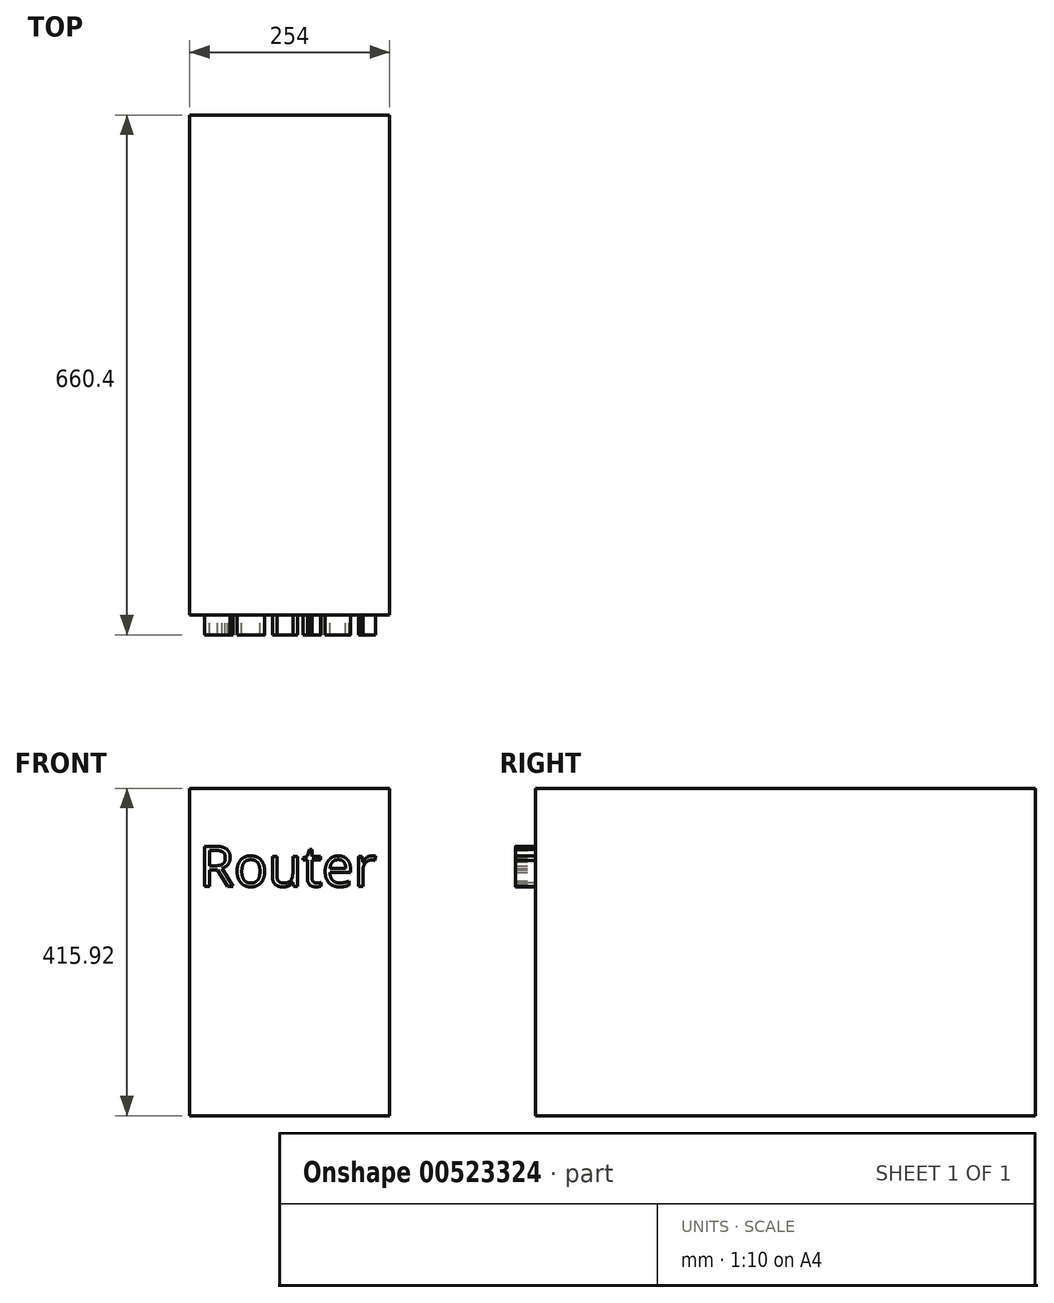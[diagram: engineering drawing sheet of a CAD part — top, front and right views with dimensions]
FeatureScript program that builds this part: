
annotation { "Feature Type Name" : "Feature", "Feature Type Description" : "" }
export const myFeature = defineFeature(function(context is Context, id is Id, definition is map)
    precondition{}
    {
        {
            var Q0;
            Q0=qCreatedBy(makeId("Front.planeOp"),FACE);
            var sketch = newSketch(context, id + "F0", { "sketchPlane" : qUnion([Q0])});
            skLineSegment(sketch, "E0.bottom", {"start": v(127, 207.96) * mm, "end": v(-127, 207.96) * mm});
            skLineSegment(sketch, "E0.top", {"start": v(127, -207.96) * mm, "end": v(-127, -207.96) * mm});
            skLineSegment(sketch, "E0.left", {"start": v(127, 207.96) * mm, "end": v(127, -207.96) * mm});
            skLineSegment(sketch, "E0.right", {"start": v(-127, 207.96) * mm, "end": v(-127, -207.96) * mm});
            skPoint(sketch, "E0.middle", {"position": v(0, 0) * mm});
            skSolve(sketch);
        }
        {
            var Q0;
            Q0=makeQuery(id+"F0.imprint","IMPRINT",FACE,{"disambiguationData":[TD([[makeQuery(id+"F0.imprint","IMPRINT",EDGE,{"derivedFrom":sQuery(id+"F0.wireOp",EDGE,"E0.bottom")}),1.0]])]});
            extrude(context, id + "F1", {"entities" : qUnion([Q0]), "depth" : 635 * mm, "offsetDistance" : 25.4 * mm});
        }
        {
            var Q0;
            Q0=makeQuery(id+"F1.opExtrude","CAP_FACE",FACE,{"disambiguationData":[OSD([sQuery(id+"F0.wireOp",EDGE,"E0.bottom"),sQuery(id+"F0.wireOp",EDGE,"E0.top"),sQuery(id+"F0.wireOp",EDGE,"E0.left"),sQuery(id+"F0.wireOp",EDGE,"E0.right")])],"isStart":false});
            var sketch = newSketch(context, id + "F2", { "sketchPlane" : qUnion([Q0])});
            skText(sketch, "E1", { "text": "Router", "fontName": "OpenSans-Regular.ttf"});
            const initialGuessF2  = {"E1": [-0.115, 0.08333, 1, 0, 0.0513]};
            skSetInitialGuess(sketch, initialGuessF2);
            skSolve(sketch);
        }
        {
            var Q0;
            Q0 = qSketchRegion(id + "F2", true);
            extrude(context, id + "F3", {"entities" : qUnion([Q0]), "operationType" : NewBodyOperationType.ADD, "depth" : 25.4 * mm, "offsetDistance" : 25.4 * mm});
        }
    });
